# Revit family: Cruiserweight-NI-LH-312P
name_source: partatom
category: Generic Models
units: mm (PartAtom-declared; Revit-internal decimal feet)

## family parameters
Always vertical = Yes
Can host rebar = No
Cut with Voids When Loaded = Yes
Host = Wall
Maintain Annotation Orientation = No
Part Type = Normal
Room Calculation Point = No
Round Connector Dimension = Use Diameter
Shared = No

## types (9) — shared parameters
Default Elevation = 0' - 0"
Description = Sectional Doors
DoorThk = 0' - 0 3/4"
HeadRoom = 3' - 0"
Manufacturer = TKO
Model = Cruiserweight
PanelSize = 2' - 0"
TrackDepth = 0' - 5 3/8"
TrackWidth = 0' - 3 1/2"
Type Comments = Non-Insulated
URL = https://kelleyentrematic.com

## per-type parameters (varying)
| type | HorizTrack | OpeningHeight | OpeningWidth | TrackHeight | VerticalTrack |
| 8' x 10' | 9' - 0" | 10' - 0" | 8' - 0" | 13' - 0" | 11' - 6" |
| 9' x 10' | 9' - 0" | 10' - 0" | 9' - 0" | 13' - 0" | 11' - 6" |
| 10' x 10' | 9' - 0" | 10' - 0" | 10' - 0" | 13' - 0" | 11' - 6" |
| 10' x 8' | 7' - 0" | 8' - 0" | 10' - 0" | 11' - 0" | 9' - 6" |
| 10' x 9' | 8' - 0" | 9' - 0" | 10' - 0" | 12' - 0" | 10' - 6" |
| 8' x 9' | 8' - 0" | 9' - 0" | 8' - 0" | 12' - 0" | 10' - 6" |
| 8' x 8' | 7' - 0" | 8' - 0" | 8' - 0" | 11' - 0" | 9' - 6" |
| 9' x 9' | 8' - 0" | 9' - 0" | 9' - 0" | 12' - 0" | 10' - 6" |
| 9' x 8' | 8' - 0" | 9' - 0" | 9' - 0" | 12' - 0" | 10' - 6" |

## geometry (parser evidence)
native form markers: Sweep x3
no freeform markers — native parametric forms only
